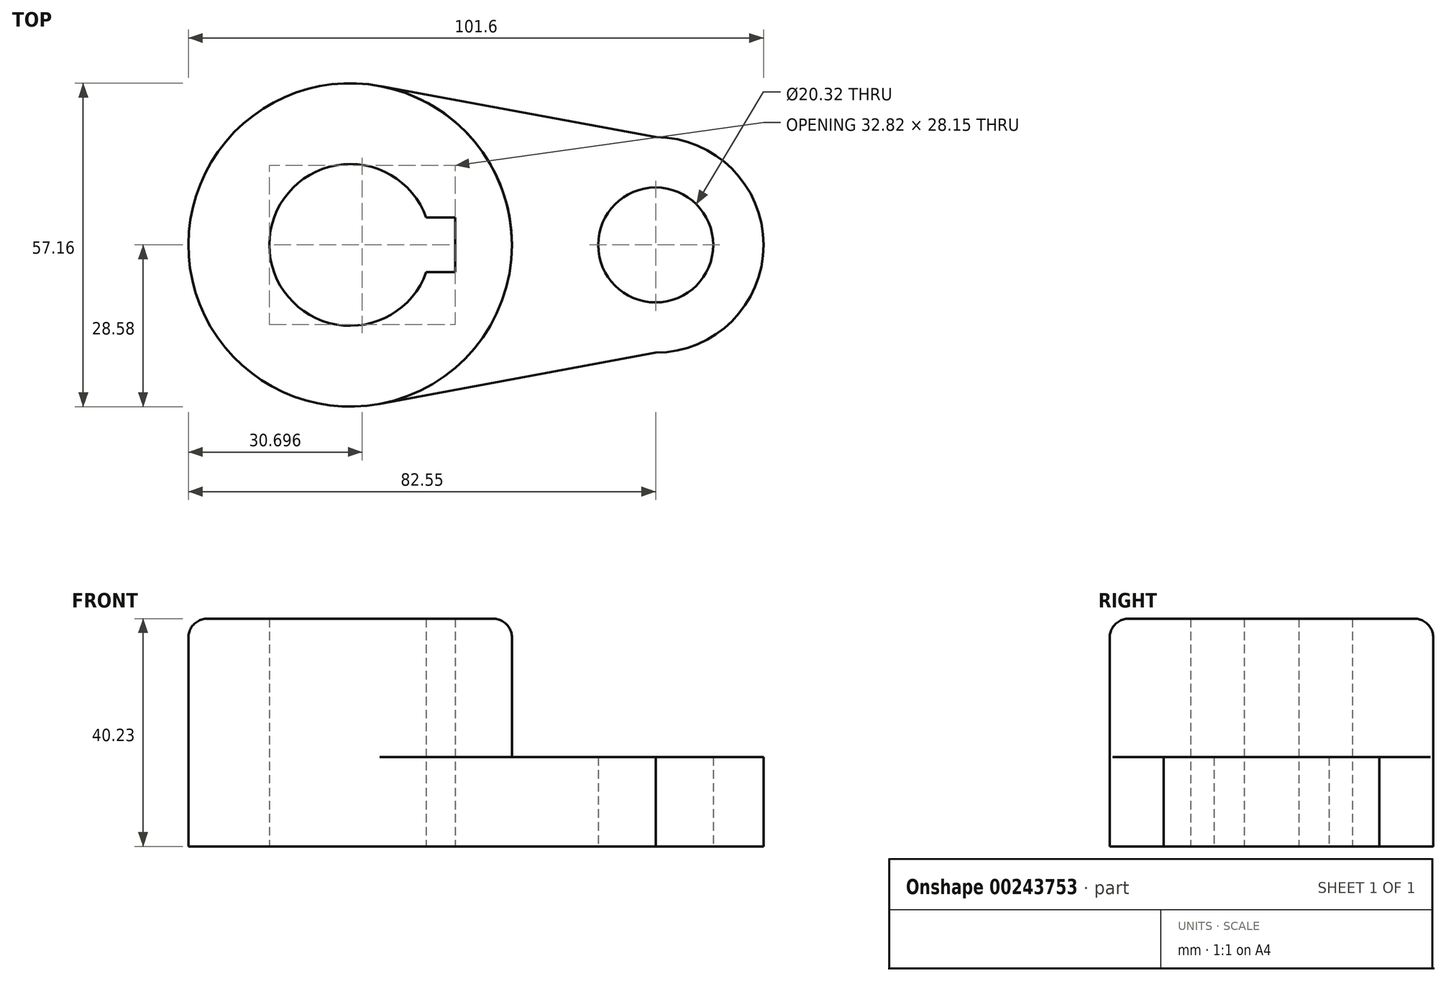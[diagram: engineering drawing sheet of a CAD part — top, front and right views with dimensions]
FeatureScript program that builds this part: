
annotation { "Feature Type Name" : "Feature", "Feature Type Description" : "" }
export const myFeature = defineFeature(function(context is Context, id is Id, definition is map)
    precondition{}
    {
        {
            var Q0;
            Q0=qCreatedBy(makeId("Top.planeOp"),FACE);
            var sketch = newSketch(context, id + "F0", { "sketchPlane" : qUnion([Q0])});
            skCircle(sketch, "E0", {"center": v(-31.05, 0) * mm, "radius": 28.58 * mm});
            skCircle(sketch, "E1", {"center": v(-31.05, 0) * mm, "radius": 14.29 * mm});
            skLineSegment(sketch, "E2.bottom", {"start": v(-12.53, -4.83) * mm, "end": v(-49.58, -4.83) * mm});
            skLineSegment(sketch, "E2.top", {"start": v(-12.53, 4.83) * mm, "end": v(-49.58, 4.83) * mm});
            skLineSegment(sketch, "E2.left", {"start": v(-12.53, -4.83) * mm, "end": v(-12.53, 4.83) * mm});
            skLineSegment(sketch, "E2.right", {"start": v(-49.58, -4.83) * mm, "end": v(-49.58, 4.83) * mm});
            skCircle(sketch, "E3", {"center": v(22.92, 0) * mm, "radius": 10.16 * mm});
            skPoint(sketch, "E3.centerSnap0", {"position": v(-12.53, 0) * mm});
            skArc(sketch, "E4", {"start": v(22.92, 19.05) * mm, "mid": v(41.97, 0) * mm, "end": v(22.92, -19.05) * mm});
            skLineSegment(sketch, "E5", {"start": v(22.92, 19.05) * mm, "end": v(-31.05, 29.06) * mm});
            skPoint(sketch, "E5.endSnap0", {"position": v(-31.05, 4.83) * mm});
            skLineSegment(sketch, "E6", {"start": v(22.92, -19.05) * mm, "end": v(-31.05, -29.06) * mm});
            skSolve(sketch);
        }
        {
            var Q0;
            {var subQ7=sQuery(id+"F0.wireOp",EDGE,"E2.left");Q0=makeQuery(id+"F0.imprint","IMPRINT",FACE,{"disambiguationData":[TD([[makeQuery(id+"F0.imprint","IMPRINT",EDGE,{"derivedFrom":subQ7}),-1.0]])]});}
            var Q1;
            {var subQ5=sQuery(id+"F0.wireOp",EDGE,"E2.right");Q1=makeQuery(id+"F0.imprint","IMPRINT",FACE,{"disambiguationData":[TD([[makeQuery(id+"F0.imprint","IMPRINT",EDGE,{"derivedFrom":subQ5}),-1.0]])]});}
            extrude(context, id + "F1", {"entities" : qUnion([Q0, Q1]), "depth" : 40.23 * mm});
        }
        {
            var Q0;
            Q0=makeQuery(id+"F0.imprint","IMPRINT",FACE,{"disambiguationData":[TD([[makeQuery(id+"F0.imprint","IMPRINT",EDGE,{"derivedFrom":sQuery(id+"F0.wireOp",EDGE,"E3")}),-1.0]])]});
            extrude(context, id + "F2", {"entities" : qUnion([Q0]), "operationType" : NewBodyOperationType.ADD, "depth" : 15.77 * mm});
        }
        {
            var Q0;
            Q0=makeQuery(id+"F1.opExtrude","CAP_EDGE",EDGE,{"disambiguationData":[OSD([sQuery(id+"F0.wireOp",EDGE,"E0")])],"isStart":false});
            fillet(context, id + "F3", {"entities" : qUnion([Q0]), "radius" : 3.3 * mm, "tangentPropagation" : true, "allowEdgeOverflow" : false});
        }
    });
